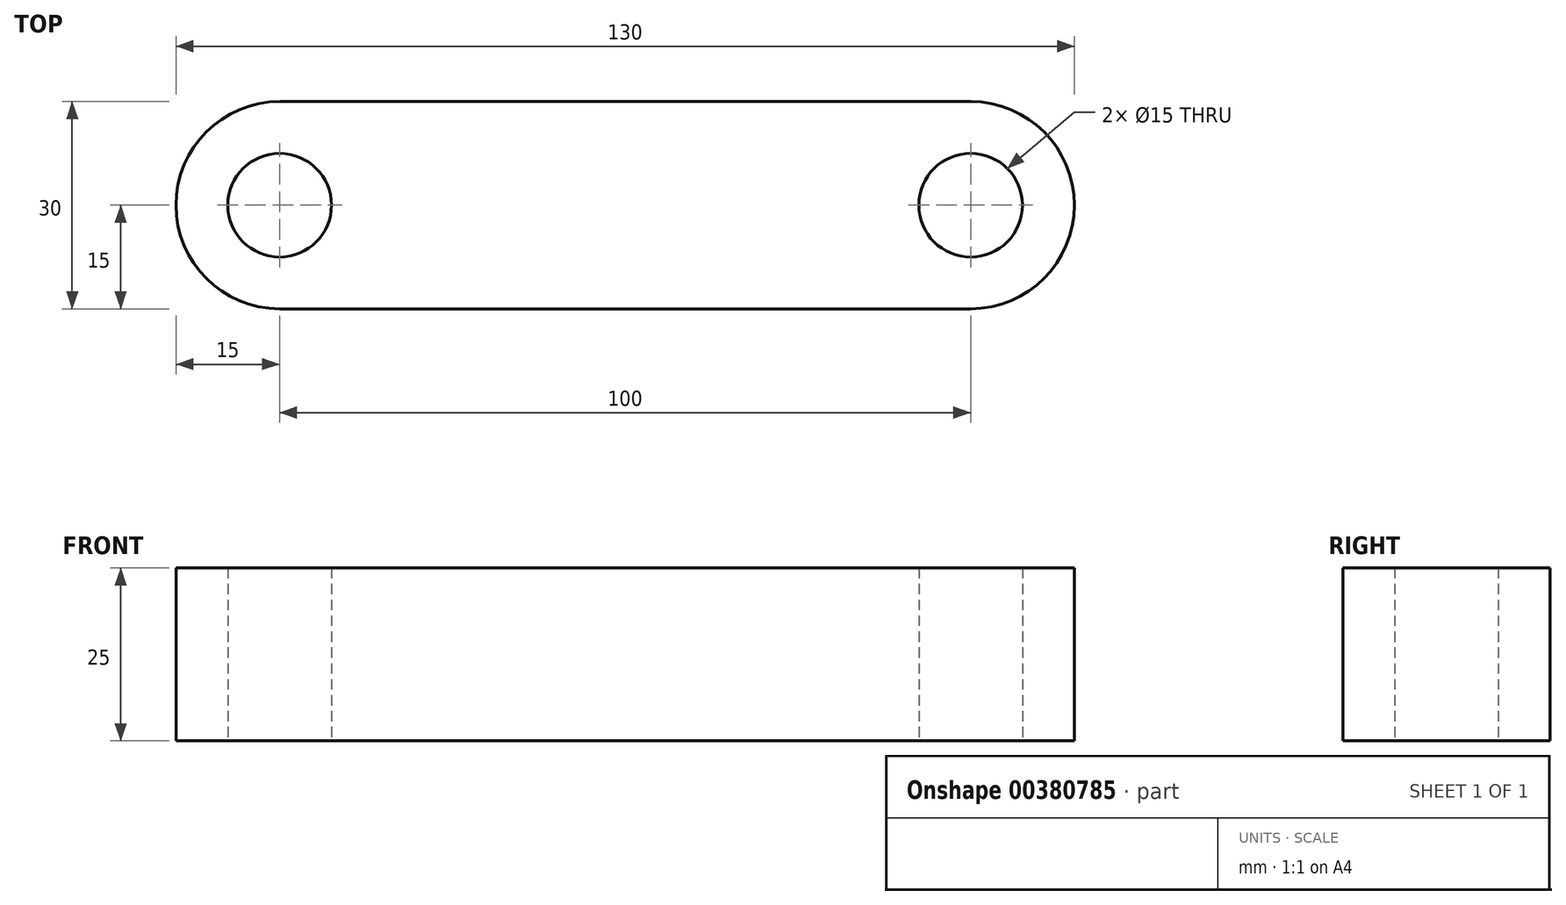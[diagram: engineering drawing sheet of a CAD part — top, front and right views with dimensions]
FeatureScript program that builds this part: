
annotation { "Feature Type Name" : "Feature", "Feature Type Description" : "" }
export const myFeature = defineFeature(function(context is Context, id is Id, definition is map)
    precondition{}
    {
        {
            var Q0;
            Q0=qCreatedBy(makeId("Top.planeOp"),FACE);
            var sketch = newSketch(context, id + "F0", { "sketchPlane" : qUnion([Q0])});
            skLineSegment(sketch, "E0", {"start": v(0, -15) * mm, "end": v(100, -15) * mm});
            skLineSegment(sketch, "E1", {"start": v(0, 15) * mm, "end": v(100, 15) * mm});
            skArc(sketch, "E2", {"start": v(0, 15) * mm, "mid": v(-15, 0) * mm, "end": v(0, -15) * mm});
            skArc(sketch, "E3", {"start": v(100, -15) * mm, "mid": v(115, 0) * mm, "end": v(100, 15) * mm});
            skCircle(sketch, "E4", {"center": v(0, 0) * mm, "radius": 7.5 * mm});
            skCircle(sketch, "E5", {"center": v(100, 0) * mm, "radius": 7.5 * mm});
            skSolve(sketch);
        }
        {
            var Q0;
            Q0=makeQuery(id+"F0.imprint","IMPRINT",FACE,{"disambiguationData":[TD([[makeQuery(id+"F0.imprint","IMPRINT",EDGE,{"derivedFrom":sQuery(id+"F0.wireOp",EDGE,"E0")}),1.0]])]});
            extrude(context, id + "F1", {"entities" : qUnion([Q0]), "depth" : 25 * mm});
        }
    });
